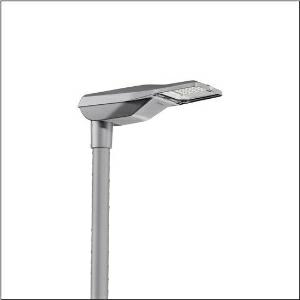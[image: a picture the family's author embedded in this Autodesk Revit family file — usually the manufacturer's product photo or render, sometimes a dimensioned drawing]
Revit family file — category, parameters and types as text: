
# Revit family: streetlight_sl_21_iq_micro___st1_5a_5xe1p41d08db_9421
name_source: partatom
category: Lighting Fixtures
units: mm (PartAtom-declared; Revit-internal decimal feet)

## family parameters
Cut with Voids When Loaded = No
Host = Face
Light Source = No
Part Type = Normal
Room Calculation Point = No
Round Connector Dimension = Use Diameter
Shared = No

## types (1)
- --- (1 x LED, 4930 lm, 36.4 W, 4000K)
    Apparent Load = 36 VA
    CIE Flux Codes = 22 53 95 100 100
    Color Rendering = 70
    Color Temperature = 4000K
    Default Elevation = 1800 mm
    Description = Streetlight SL 21 iQ micro, mast luminaire, primary light control with lens, of PMMA, primary optical cover: cover, of toughened safety glass, transparent, light distribution: ST1.5a, light emission: direct distribution, primary light characteristic: asymmetric, installation type: post-top, side-entry, LED, High Power LED, rated luminous flux: 4.930lm, luminous efficacy: 135lm/W, light colour: 740, colour temperature: 4000K, control gear: iQ-Comfort, control: Auto-Match, Temp-Guard, Lumen-Switch, Night-Set, Smart-Wire, Light-Fading, Desk-Remote (wireless, voltage-free reading and setting of iQ features in the workshop via application-optimized NFC function/RFID function), optimised constant luminous flux control (CLO 2.0), pre-setting: linear dimming characteristic, mains connection: 220..240V, AC, 50/60Hz, start of lifetime: 36W, end of service life: 38W, reduction: 16W, luminaire housing, of diecast aluminium, powder-coated, SITECO metallic grey (DB 702S), corrosivity category C5 high according to DIN EN ISO 12944, please order mast flange separately, inclination adjustable: 0°, 5°, 10°, 15°, sealing non-destructively replaceable, multi-level sealing system, length: 528mm, width: 235mm, height: 110mm, mast flange for spigot size: 42mm (side-entry): 5XC10008XM4, 60/48mm (side-entry/post-top): 5XC10108XM2, 76/60mm (side-entry/post-top): 5XC10108XM1, protection rating (complete): IP66, insulation class (complete): insulation class II (safety insulation), certification: CE, ENEC, ENEC+, VDE, impact resistance: IK10, permissible operating ambient temperature for outdoor applications: -40..+50°C, standard-compliant lighting for roads and squares, packaging unit: 1 piece

Light Distribution: ST1.5a
    Height = 110 mm
    Lamp = 1 x LED
    Lamp Light Flux = 4930 lm
    Lamp Power = 36.4 W
    Lamp count = 1
    Length = 528 mm
    Luminous efficacy = 135 lm/W
    Manufacturer = Siteco
    ModVariant = No
    Model = 5XE1P41D08DB
    Number of Poles = 1
    OnlyDefault = Yes
    Power Factor = 1
    Product Name = Streetlight SL 21 iQ micro | ST1.5a
    Product group = mast luminaire | pylon top
    ProductGroupID = 6100
    Protection Class = Protection class II
    Protection Degree = IP 66
    RLX_Detail_Level = 1
    RLX_Emergency_Light_Flux = 0 lm
    RLX_Emergency_Type = 0
    RLX_Emergency_Type_DB = No
    RlxData = <blob elided: 103349 chars, md5=756bdf62>
    Socket = socket
    Standby Power = 0 W
    System Light Flux = 4930 lm
    System Power = 36 W
    Type Comments = factory setting: luminous flux: 100 % | dim-lin: 254 | 715 mA
    Type Image = l_1006881.jpg
    URL = http://relux.com
    VarID = @adj_153317
    Voltage = 0 V
    Weight = 0.00 kg
    Width = 235 mm

## geometry (parser evidence)
native form markers: Blend x4, Sweep x10
no freeform markers — native parametric forms only
